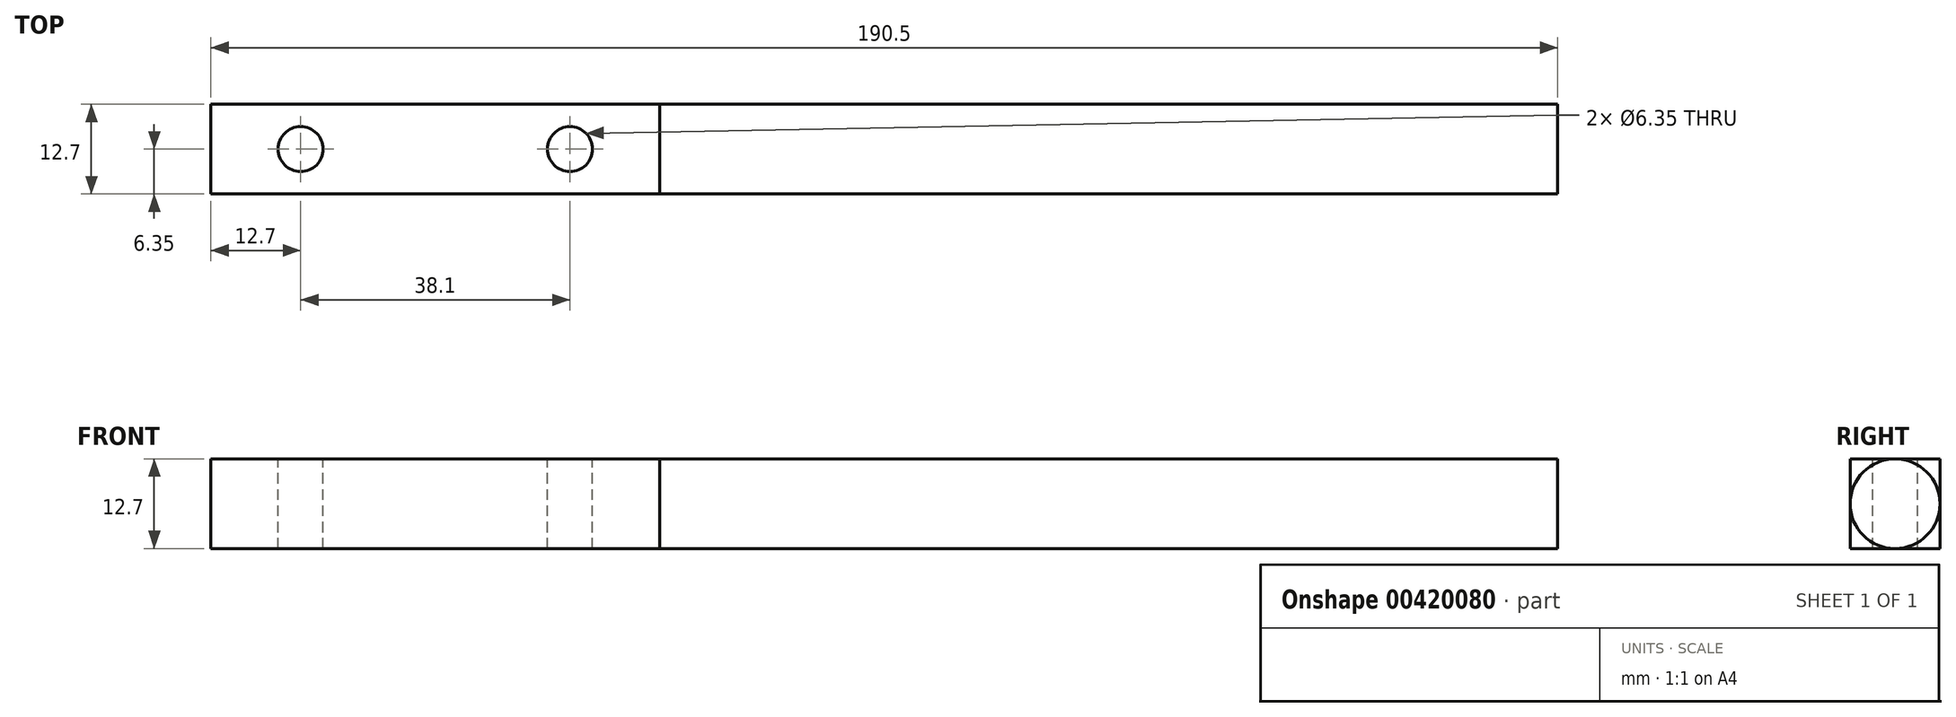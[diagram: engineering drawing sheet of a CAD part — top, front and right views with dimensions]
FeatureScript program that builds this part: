
annotation { "Feature Type Name" : "Feature", "Feature Type Description" : "" }
export const myFeature = defineFeature(function(context is Context, id is Id, definition is map)
    precondition{}
    {
        {
            var Q0;
            Q0=qCreatedBy(makeId("Right.planeOp"),FACE);
            var sketch = newSketch(context, id + "F0", { "sketchPlane" : qUnion([Q0])});
            skLineSegment(sketch, "E0.bottom", {"start": v(6.35, -6.35) * mm, "end": v(-6.35, -6.35) * mm});
            skLineSegment(sketch, "E0.top", {"start": v(6.35, 6.35) * mm, "end": v(-6.35, 6.35) * mm});
            skLineSegment(sketch, "E0.left", {"start": v(6.35, -6.35) * mm, "end": v(6.35, 6.35) * mm});
            skLineSegment(sketch, "E0.right", {"start": v(-6.35, -6.35) * mm, "end": v(-6.35, 6.35) * mm});
            skPoint(sketch, "E0.middle", {"position": v(0, 0) * mm});
            skSolve(sketch);
        }
        {
            var Q0;
            Q0=makeQuery(id+"F0.imprint","IMPRINT",FACE,{"disambiguationData":[TD([[makeQuery(id+"F0.imprint","IMPRINT",EDGE,{"derivedFrom":sQuery(id+"F0.wireOp",EDGE,"E0.bottom")}),-1.0]])]});
            extrude(context, id + "F1", {"entities" : qUnion([Q0]), "oppositeDirection" : true, "depth" : 63.5 * mm});
        }
        {
            var Q0;
            Q0=qCreatedBy(makeId("Right.planeOp"),FACE);
            var sketch = newSketch(context, id + "F2", { "sketchPlane" : qUnion([Q0])});
            skCircle(sketch, "E1", {"center": v(0, 0) * mm, "radius": 6.35 * mm});
            skSolve(sketch);
        }
        {
            var Q0;
            Q0 = qSketchRegion(id + "F2", true);
            extrude(context, id + "F3", {"entities" : qUnion([Q0]), "operationType" : NewBodyOperationType.ADD, "depth" : 127 * mm});
        }
        {
            var Q0;
            Q0=makeQuery(id+"F1.opExtrude","SWEPT_FACE",FACE,{"disambiguationData":[OSD([sQuery(id+"F0.wireOp",EDGE,"E0.top")])]});
            var sketch = newSketch(context, id + "F4", { "sketchPlane" : qUnion([Q0])});
            skCircle(sketch, "E2", {"center": v(-50.8, 0) * mm, "radius": 3.18 * mm});
            skPoint(sketch, "E2.centerSnap0", {"position": v(-63.5, 0) * mm});
            skCircle(sketch, "E3", {"center": v(-12.7, 0) * mm, "radius": 3.18 * mm});
            skSolve(sketch);
        }
        {
            var Q0;
            Q0 = qSketchRegion(id + "F4", true);
            extrude(context, id + "F5", {"entities" : qUnion([Q0]), "operationType" : NewBodyOperationType.REMOVE, "oppositeDirection" : true, "depth" : 12.7 * mm});
        }
    });
